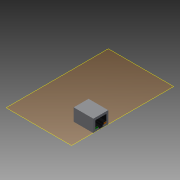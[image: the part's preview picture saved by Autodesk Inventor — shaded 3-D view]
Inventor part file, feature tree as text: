
AUTODESK INVENTOR PART (.ipt)
format: ipt  version: 2013 SP2 (Build 170200200, 200)  size: 138,240 bytes
history: native  units: mm
features: extrude x3, sketch x3, plane x1
ambient origin geometry x8: Origin, YZ Plane, XZ Plane, XY Plane, X Axis, Y Axis, Z Axis, Center Point
bodies: Solid1 (feature_tree)
feature tree (7):
  plane  "Work Plane1"
  extrude  "Extrusion1"  Depth=16.0mm
  extrude  "Extrusion2"  Depth=2.0mm
  extrude  "Extrusion3"  Depth=2.5mm
  sketch  "Sketch1"  dims[d0=21.2mm d2=16.0mm]
  sketch  "Sketch2"  dims[d3=13.4mm d4=0.0mm d5=2.0mm]
  sketch  "Sketch3"  dims[d6=2.0mm d7=2.5mm d8=5.0mm d9=6.0mm d10=1.0mm d11=2.5mm d12=4.3mm d13=11.5mm d14=0.0mm d15=0.2mm d16=0.2mm d17=0.2mm d18=0.2mm d19=0.2mm d20=0.0mm]
